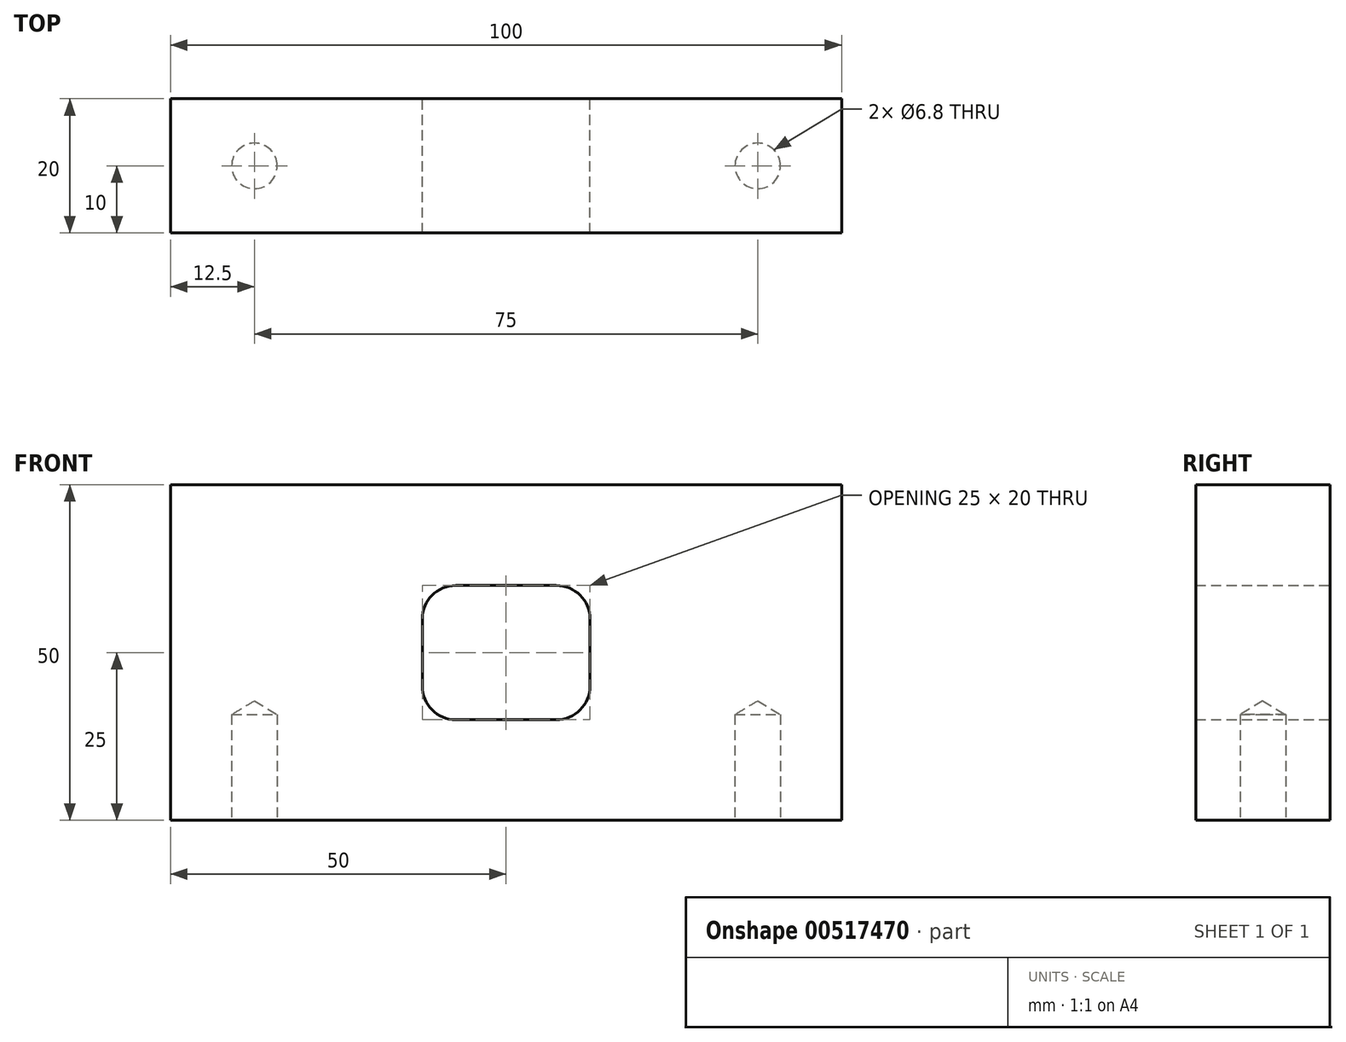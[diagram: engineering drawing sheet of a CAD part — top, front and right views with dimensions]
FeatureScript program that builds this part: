
annotation { "Feature Type Name" : "Feature", "Feature Type Description" : "" }
export const myFeature = defineFeature(function(context is Context, id is Id, definition is map)
    precondition{}
    {
        {
            var Q0;
            Q0=qCreatedBy(makeId("Front.planeOp"),FACE);
            var sketch = newSketch(context, id + "F0", { "sketchPlane" : qUnion([Q0])});
            skLineSegment(sketch, "E0", {"start": v(-50, 0) * mm, "end": v(50, 0) * mm});
            skLineSegment(sketch, "E1", {"start": v(50, 0) * mm, "end": v(50, 50) * mm});
            skLineSegment(sketch, "E2", {"start": v(50, 50) * mm, "end": v(-50, 50) * mm});
            skLineSegment(sketch, "E3", {"start": v(-50, 50) * mm, "end": v(-50, 0) * mm});
            skLineSegment(sketch, "E4.bottom", {"start": v(7.5, 15) * mm, "end": v(-7.5, 15) * mm});
            skLineSegment(sketch, "E4.top", {"start": v(7.5, 35) * mm, "end": v(-7.5, 35) * mm});
            skLineSegment(sketch, "E4.left", {"start": v(12.5, 20) * mm, "end": v(12.5, 30) * mm});
            skLineSegment(sketch, "E4.right", {"start": v(-12.5, 20) * mm, "end": v(-12.5, 30) * mm});
            skPoint(sketch, "E4.middle", {"position": v(0, 25) * mm});
            skPoint(sketch, "E5.visualSharp", {"position": v(-12.5, 35) * mm});
            skArc(sketch, "E5.filletArc", {"start": v(-7.5, 35) * mm, "mid": v(-11.04, 33.54) * mm, "end": v(-12.5, 30) * mm});
            skPoint(sketch, "E6.visualSharp", {"position": v(12.5, 35) * mm});
            skArc(sketch, "E6.filletArc", {"start": v(12.5, 30) * mm, "mid": v(11.04, 33.54) * mm, "end": v(7.5, 35) * mm});
            skPoint(sketch, "E7.visualSharp", {"position": v(12.5, 15) * mm});
            skArc(sketch, "E7.filletArc", {"start": v(7.5, 15) * mm, "mid": v(11.04, 16.46) * mm, "end": v(12.5, 20) * mm});
            skPoint(sketch, "E8.visualSharp", {"position": v(-12.5, 15) * mm});
            skArc(sketch, "E8.filletArc", {"start": v(-12.5, 20) * mm, "mid": v(-11.04, 16.46) * mm, "end": v(-7.5, 15) * mm});
            skSolve(sketch);
        }
        {
            var Q0;
            Q0=makeQuery(id+"F0.imprint","IMPRINT",FACE,{"disambiguationData":[TD([[makeQuery(id+"F0.imprint","IMPRINT",EDGE,{"derivedFrom":sQuery(id+"F0.wireOp",EDGE,"E0")}),1.0]])]});
            extrude(context, id + "F1", {"entities" : qUnion([Q0]), "endBound" : BoundingType.SYMMETRIC, "depth" : 20 * mm, "offsetDistance" : 25 * mm});
        }
        {
            var Q0;
            Q0=makeQuery(id+"F1.opExtrude","SWEPT_FACE",FACE,{"disambiguationData":[OSD([sQuery(id+"F0.wireOp",EDGE,"E0")])]});
            var sketch = newSketch(context, id + "F2", { "sketchPlane" : qUnion([Q0])});
            skLineSegment(sketch, "E9", {"start": v(-37.5, 0) * mm, "end": v(37.5, 0) * mm});
            skSolve(sketch);
        }
        {
            var Q0;
            Q0=sQuery(id+"F2.wireOp",VERTEX,"E9.start");
            var Q1;
            Q1=sQuery(id+"F2.wireOp",VERTEX,"E9.end");
            var Q2;
            Q2=makeQuery(id+"F1.opExtrude","SWEPT_BODY",BODY,{"disambiguationData":[OSD([sQuery(id+"F0.wireOp",EDGE,"E0"),sQuery(id+"F0.wireOp",EDGE,"E1"),sQuery(id+"F0.wireOp",EDGE,"E2"),sQuery(id+"F0.wireOp",EDGE,"E3"),sQuery(id+"F0.wireOp",EDGE,"E4.bottom"),sQuery(id+"F0.wireOp",EDGE,"E4.top"),sQuery(id+"F0.wireOp",EDGE,"E4.left"),sQuery(id+"F0.wireOp",EDGE,"E4.right"),sQuery(id+"F0.wireOp",EDGE,"E5.filletArc"),sQuery(id+"F0.wireOp",EDGE,"E6.filletArc"),sQuery(id+"F0.wireOp",EDGE,"E7.filletArc"),sQuery(id+"F0.wireOp",EDGE,"E8.filletArc")])]});
            hole(context, id + "F3", {"style" : HoleStyle.SIMPLE, "endStyle" : HoleEndStyle.BLIND, "standardTappedOrClearance" : lookupTablePath({ "standard" : "ISO", "engagement" : "75%", "pitch" : "1.25 mm", "size" : "M8", "type" : "Tapped" }), "standardBlindInLast" : lookupTablePath({ "standard" : "ISO", "engagement" : "75%", "pitch" : "1.25 mm", "size" : "M8", "type" : "Tapped" }), "holeDiameter" : 6.8 * mm, "showTappedDepth" : true, "holeDepth" : 15.75 * mm, "isTappedThrough" : true, "tappedDepth" : 12 * mm, "tapClearance" : 3, "locations" : qUnion([Q0, Q1]), "scope" : qUnion([Q2]), "majorDiameter" : 8 * mm});
        }
    });
